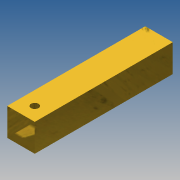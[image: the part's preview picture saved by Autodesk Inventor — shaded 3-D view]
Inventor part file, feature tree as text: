
AUTODESK INVENTOR PART (.ipt)
format: ipt  version: 2014 SP1 (Build 180222100, 222)  size: 84,480 bytes
history: native  units: in
note: dims shown in document units (in); Inventor stores cm internally (conversion verified against a paired STEP export)
features: extrude x2, sketch x2
ambient origin geometry x8: Origin, YZ Plane, XZ Plane, XY Plane, X Axis, Y Axis, Z Axis, Center Point
bodies: Solid1 (feature_tree)
feature tree (4):
  extrude  "Extrusion1"  Depth=10.0in
  extrude  "Extrusion2"  Depth=1.0in
  sketch  "Sketch1"  dims[d0=2.0in d1=10.0in]
  sketch  "Sketch2"  dims[d2=2.0in d3=0.0in d4=1.0in d5=1.0in d6=0.0in]
